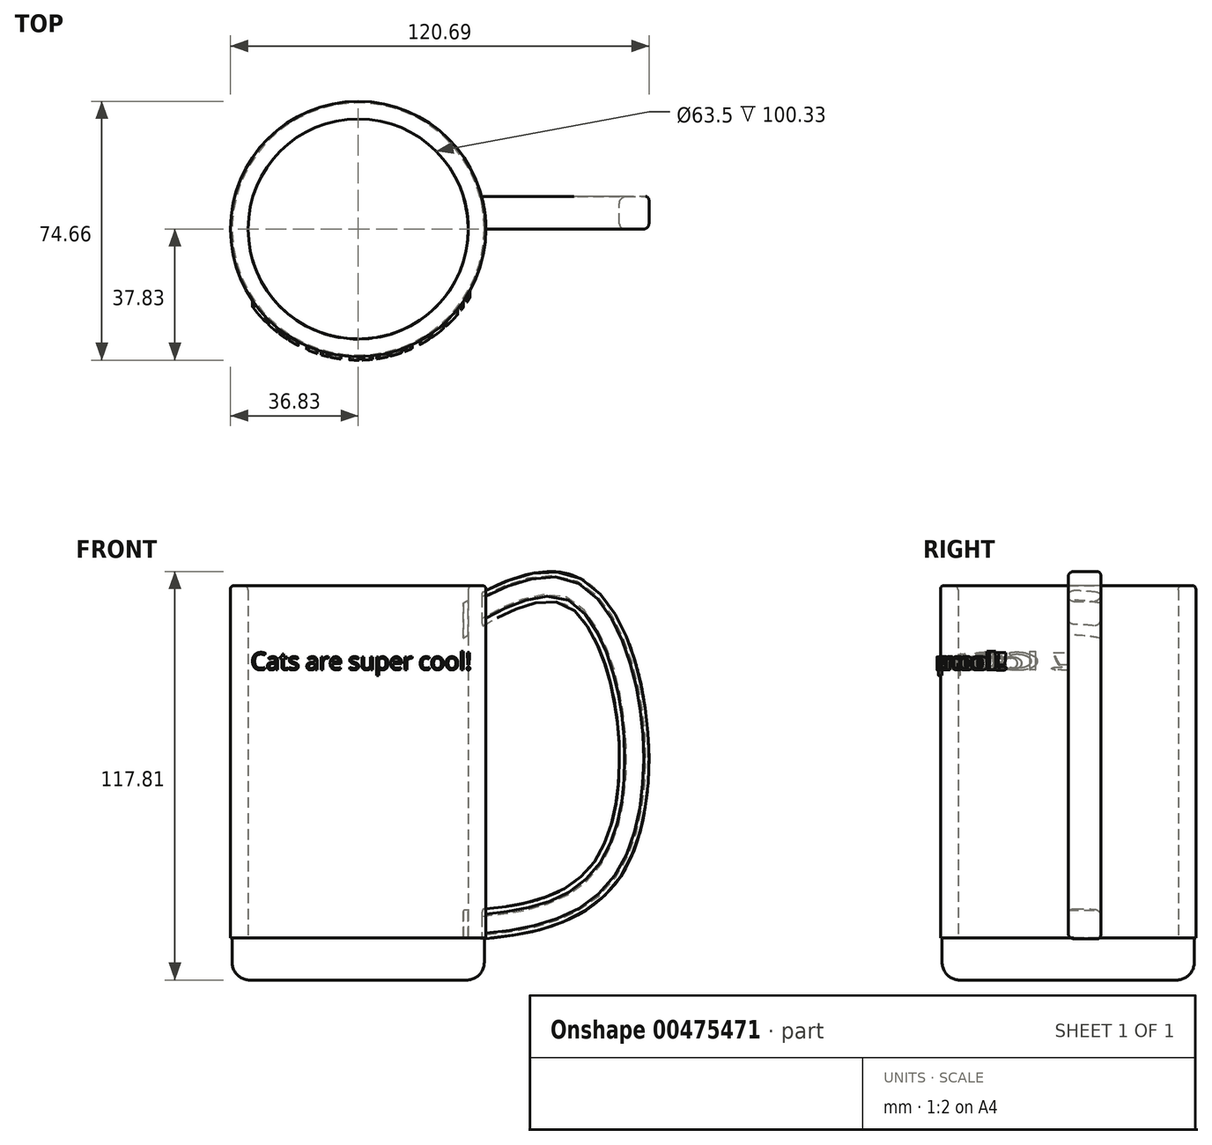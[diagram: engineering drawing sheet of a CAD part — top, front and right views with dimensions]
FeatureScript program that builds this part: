
annotation { "Feature Type Name" : "Feature", "Feature Type Description" : "" }
export const myFeature = defineFeature(function(context is Context, id is Id, definition is map)
    precondition{}
    {
        {
            var Q0;
            Q0=qCreatedBy(makeId("Top.planeOp"),FACE);
            var sketch = newSketch(context, id + "F0", { "sketchPlane" : qUnion([Q0])});
            skCircle(sketch, "E0", {"center": v(0, 0) * mm, "radius": 31.75 * mm});
            skCircle(sketch, "E1.0", {"center": v(0, 0) * mm, "radius": 36.83 * mm});
            skSolve(sketch);
        }
        {
            var Q0;
            Q0 = qSketchRegion(id + "F0", true);
            extrude(context, id + "F1", {"entities" : qUnion([Q0]), "depth" : 101.6 * mm});
        }
        {
            var Q0;
            Q0=qCreatedBy(makeId("Top.planeOp"),FACE);
            var sketch = newSketch(context, id + "F2", { "sketchPlane" : qUnion([Q0])});
            skCircle(sketch, "E2", {"center": v(0, 0) * mm, "radius": 36.63 * mm});
            skSolve(sketch);
        }
        {
            var Q0;
            Q0=qCreatedBy(makeId("Front.planeOp"),FACE);
            var sketch = newSketch(context, id + "F3", { "sketchPlane" : qUnion([Q0])});
            skText(sketch, "E3", { "text": "Cats are super cool!\n", "fontName": "OpenSans-Regular.ttf"});
            const initialGuessF3  = {"E3": [-0.0309, 0.07732, 1, 0, 0.00498]};
            skSetInitialGuess(sketch, initialGuessF3);
            skSolve(sketch);
        }
        {
            var Q0;
            Q0 = qSketchRegion(id + "F3", true);
            extrude(context, id + "F4", {"entities" : qUnion([Q0]), "operationType" : NewBodyOperationType.ADD, "depth" : 42.67 * mm});
        }
        {
            var Q0;
            Q0=makeQuery(id+"F1.opExtrude","CAP_FACE",FACE,{"disambiguationData":[OSD([sQuery(id+"F0.wireOp",EDGE,"E0"),sQuery(id+"F0.wireOp",EDGE,"E1.0")])],"isStart":false});
            var sketch = newSketch(context, id + "F5", { "sketchPlane" : qUnion([Q0])});
            skCircle(sketch, "E4", {"center": v(0, 0) * mm, "radius": 31.34 * mm});
            skSolve(sketch);
        }
        {
            var Q0;
            Q0 = qSketchRegion(id + "F5", true);
            extrude(context, id + "F6", {"entities" : qUnion([Q0]), "operationType" : NewBodyOperationType.REMOVE, "oppositeDirection" : true, "depth" : 91.44 * mm});
        }
        {
            var Q0;
            Q0=qCreatedBy(makeId("Front.planeOp"),FACE);
            var sketch = newSketch(context, id + "F7", { "sketchPlane" : qUnion([Q0])});
            skLineSegment(sketch, "E5.0", {"start": v(-36.83, 101.6) * mm, "end": v(36.83, 101.6) * mm});
            skLineSegment(sketch, "E6", {"start": v(36.83, 101.6) * mm, "end": v(36.83, 0) * mm});
            skLineSegment(sketch, "E7", {"start": v(36.63, 0) * mm, "end": v(36.63, -7.87) * mm});
            skLineSegment(sketch, "E8.0", {"start": v(-36.63, -7.87) * mm, "end": v(36.63, -7.87) * mm});
            skLineSegment(sketch, "E9.0", {"start": v(-36.83, 0) * mm, "end": v(36.83, 0) * mm});
            skLineSegment(sketch, "E10.0", {"start": v(-36.83, -1) * mm, "end": v(37.83, -1) * mm});
            skLineSegment(sketch, "E10.1", {"start": v(37.83, 102.6) * mm, "end": v(37.83, -1) * mm});
            skLineSegment(sketch, "E10.2", {"start": v(-36.83, 102.6) * mm, "end": v(37.83, 102.6) * mm});
            skLineSegment(sketch, "E11", {"start": v(14.5, 102.6) * mm, "end": v(41.28, 127.08) * mm});
            skLineSegment(sketch, "E12", {"start": v(41.28, 127.08) * mm, "end": v(75.77, 89.35) * mm});
            skLineSegment(sketch, "E13", {"start": v(75.77, 89.35) * mm, "end": v(88.2, 29.44) * mm});
            skLineSegment(sketch, "E14", {"start": v(88.2, 29.44) * mm, "end": v(71.2, -17.18) * mm});
            skLineSegment(sketch, "E15", {"start": v(71.2, -17.18) * mm, "end": v(29.31, -25.05) * mm});
            skLineSegment(sketch, "E16", {"start": v(29.31, -25.05) * mm, "end": v(14.5, -1) * mm});
            skLineSegment(sketch, "E17", {"start": v(0, 132.94) * mm, "end": v(0, 0) * mm, "construction": true});
            skPoint(sketch, "E18", {"position": v(0, 101.6) * mm});
            skSolve(sketch);
        }
        {
            var Q0;
            Q0 = qSketchRegion(id + "F7", true);
            var Q1;
            Q1=sQuery(id+"F7.wireOp",EDGE,"E17");
            revolve(context, id + "F8", {"operationType" : NewBodyOperationType.REMOVE, "entities" : qUnion([Q0]), "axis" : qUnion([Q1]), "revolveType" : RevolveType.FULL, "oppositeDirection" : true});
        }
        {
            var Q0;
            Q0=qCreatedBy(makeId("Top.planeOp"),FACE);
            var sketch = newSketch(context, id + "F9", { "sketchPlane" : qUnion([Q0])});
            skCircle(sketch, "E19", {"center": v(0, 0) * mm, "radius": 36.37 * mm});
            skSolve(sketch);
        }
        {
            var Q0;
            Q0 = qSketchRegion(id + "F9", true);
            extrude(context, id + "F10", {"entities" : qUnion([Q0]), "operationType" : NewBodyOperationType.ADD, "oppositeDirection" : true, "depth" : 12.2 * mm});
        }
        {
            var Q0;
            Q0=qCreatedBy(makeId("Front.planeOp"),FACE);
            var sketch = newSketch(context, id + "F11", { "sketchPlane" : qUnion([Q0])});
            skFitSpline(sketch, "E20", {"points": [v(0, 74.8) * mm, v(66.28, 102.3) * mm, v(76.75, 19.41) * mm, v(0, 0) * mm], "startDerivative": vector(236.1, 181.97) * mm, "endDerivative": vector(-284.91, 12.72) * mm});
            skFitSpline(sketch, "E21.0", {"points": [v(5.27, 67.96) * mm, v(10.2, 71.75) * mm, v(17.5, 77.38) * mm, v(26.84, 84.07) * mm, v(33.57, 88.5) * mm, v(39.92, 92.16) * mm, v(45.75, 94.89) * mm, v(50.03, 96.28) * mm, v(52.99, 96.85) * mm, v(54.95, 97.02) * mm, v(56.67, 96.96) * mm, v(58.15, 96.71) * mm, v(59.48, 96.28) * mm, v(60.42, 95.81) * mm, v(61.05, 95.41) * mm, v(61.47, 95.12) * mm, v(62.02, 94.7) * mm, v(62.71, 94.08) * mm, v(63.67, 93.12) * mm, v(64.9, 91.64) * mm, v(66.39, 89.45) * mm, v(67.83, 86.87) * mm, v(69.66, 82.98) * mm, v(71.69, 77.37) * mm, v(73.56, 69.78) * mm, v(74.8, 61.68) * mm, v(75.33, 53.38) * mm, v(75.12, 45.21) * mm, v(74.15, 37.5) * mm, v(72.73, 31.73) * mm, v(71.26, 27.68) * mm, v(70.22, 25.42) * mm, v(69.32, 23.8) * mm, v(68.39, 22.28) * mm, v(67.12, 20.54) * mm, v(65.44, 18.68) * mm, v(62.98, 16.46) * mm, v(59.42, 14.09) * mm, v(54.3, 11.8) * mm, v(48.33, 10.07) * mm, v(41.58, 8.88) * mm, v(31.71, 7.95) * mm, v(18.05, 7.84) * mm, v(6.32, 8.36) * mm, v(0.39, 8.63) * mm]});
            skLineSegment(sketch, "E22", {"start": v(5.27, 67.96) * mm, "end": v(0, 74.8) * mm});
            skLineSegment(sketch, "E23", {"start": v(0.39, 8.63) * mm, "end": v(0, 0) * mm});
            skSolve(sketch);
        }
        {
            var Q0;
            Q0 = qSketchRegion(id + "F11", true);
            extrude(context, id + "F12", {"entities" : qUnion([Q0]), "operationType" : NewBodyOperationType.ADD, "oppositeDirection" : true, "depth" : 9.4 * mm});
        }
        {
            var Q0;
            Q0=makeQuery(id+"F1.opExtrude","CAP_FACE",FACE,{"disambiguationData":[OSD([sQuery(id+"F0.wireOp",EDGE,"E0"),sQuery(id+"F0.wireOp",EDGE,"E1.0")])],"isStart":false});
            var sketch = newSketch(context, id + "F13", { "sketchPlane" : qUnion([Q0])});
            skCircle(sketch, "E24", {"center": v(0, 0) * mm, "radius": 31.71 * mm});
            skSolve(sketch);
        }
        {
            var Q0;
            Q0 = qSketchRegion(id + "F13", true);
            extrude(context, id + "F14", {"entities" : qUnion([Q0]), "operationType" : NewBodyOperationType.REMOVE, "oppositeDirection" : true, "depth" : 101.6 * mm});
        }
        {
            var Q0;
            {var subQ0=sQuery(id+"F11.wireOp",EDGE,"E20");Q0=makeQuery(id+"F12.boolean.opBoolean","SPLIT",EDGE,{"disambiguationData":[TD([makeQuery(id+"F1.opExtrude","SWEPT_FACE",FACE,{"disambiguationData":[OSD([sQuery(id+"F0.wireOp",EDGE,"E1.0")])]})])],"derivedFrom":makeQuery(id+"F12.opExtrude","CAP_EDGE",EDGE,{"disambiguationData":[OSD([subQ0])],"isStart":false})});}
            fillet(context, id + "F15", {"entities" : qUnion([Q0]), "radius" : 1.02 * mm, "tangentPropagation" : true, "allowEdgeOverflow" : false});
        }
        {
            var Q0;
            {var subQ0=sQuery(id+"F11.wireOp",EDGE,"E21.0");Q0=makeQuery(id+"F12.boolean.opBoolean","SPLIT",EDGE,{"disambiguationData":[TD([makeQuery(id+"F1.opExtrude","SWEPT_FACE",FACE,{"disambiguationData":[OSD([sQuery(id+"F0.wireOp",EDGE,"E1.0")])]})])],"derivedFrom":makeQuery(id+"F12.opExtrude","CAP_EDGE",EDGE,{"disambiguationData":[OSD([subQ0])],"isStart":false})});}
            fillet(context, id + "F16", {"entities" : qUnion([Q0]), "radius" : 2.03 * mm, "tangentPropagation" : true, "allowEdgeOverflow" : false});
        }
        {
            var Q0;
            {var subQ0=sQuery(id+"F11.wireOp",EDGE,"E20");Q0=makeQuery(id+"F12.boolean.opBoolean","SPLIT",EDGE,{"disambiguationData":[TD([makeQuery(id+"F1.opExtrude","SWEPT_FACE",FACE,{"disambiguationData":[OSD([sQuery(id+"F0.wireOp",EDGE,"E1.0")])]})])],"derivedFrom":makeQuery(id+"F12.opExtrude","CAP_EDGE",EDGE,{"disambiguationData":[OSD([subQ0])],"isStart":true})});}
            var Q1;
            {var subQ0=sQuery(id+"F11.wireOp",EDGE,"E21.0");Q1=makeQuery(id+"F12.boolean.opBoolean","SPLIT",EDGE,{"disambiguationData":[TD([makeQuery(id+"F1.opExtrude","SWEPT_FACE",FACE,{"disambiguationData":[OSD([sQuery(id+"F0.wireOp",EDGE,"E1.0")])]})])],"derivedFrom":makeQuery(id+"F12.opExtrude","CAP_EDGE",EDGE,{"disambiguationData":[OSD([subQ0])],"isStart":true})});}
            fillet(context, id + "F17", {"entities" : qUnion([Q0, Q1]), "radius" : 1.52 * mm, "tangentPropagation" : true, "allowEdgeOverflow" : false});
        }
        {
            var Q0;
            Q0=makeQuery(id+"F10.opExtrude","CAP_EDGE",EDGE,{"disambiguationData":[OSD([sQuery(id+"F9.wireOp",EDGE,"E19")])],"isStart":false});
            fillet(context, id + "F18", {"entities" : qUnion([Q0]), "radius" : 5.08 * mm, "tangentPropagation" : true, "allowEdgeOverflow" : false});
        }
        {
            var Q0;
            Q0=makeQuery(id+"F1.opExtrude","CAP_EDGE",EDGE,{"disambiguationData":[OSD([sQuery(id+"F0.wireOp",EDGE,"E1.0")])],"isStart":false});
            fillet(context, id + "F19", {"entities" : qUnion([Q0]), "radius" : 1.02 * mm, "tangentPropagation" : true, "allowEdgeOverflow" : false});
        }
        {
            var Q0;
            Q0=makeQuery(id+"F1.opExtrude","CAP_EDGE",EDGE,{"disambiguationData":[OSD([sQuery(id+"F0.wireOp",EDGE,"E0")])],"isStart":false});
            fillet(context, id + "F20", {"entities" : qUnion([Q0]), "radius" : 1.27 * mm, "tangentPropagation" : true, "allowEdgeOverflow" : false});
        }
    });
